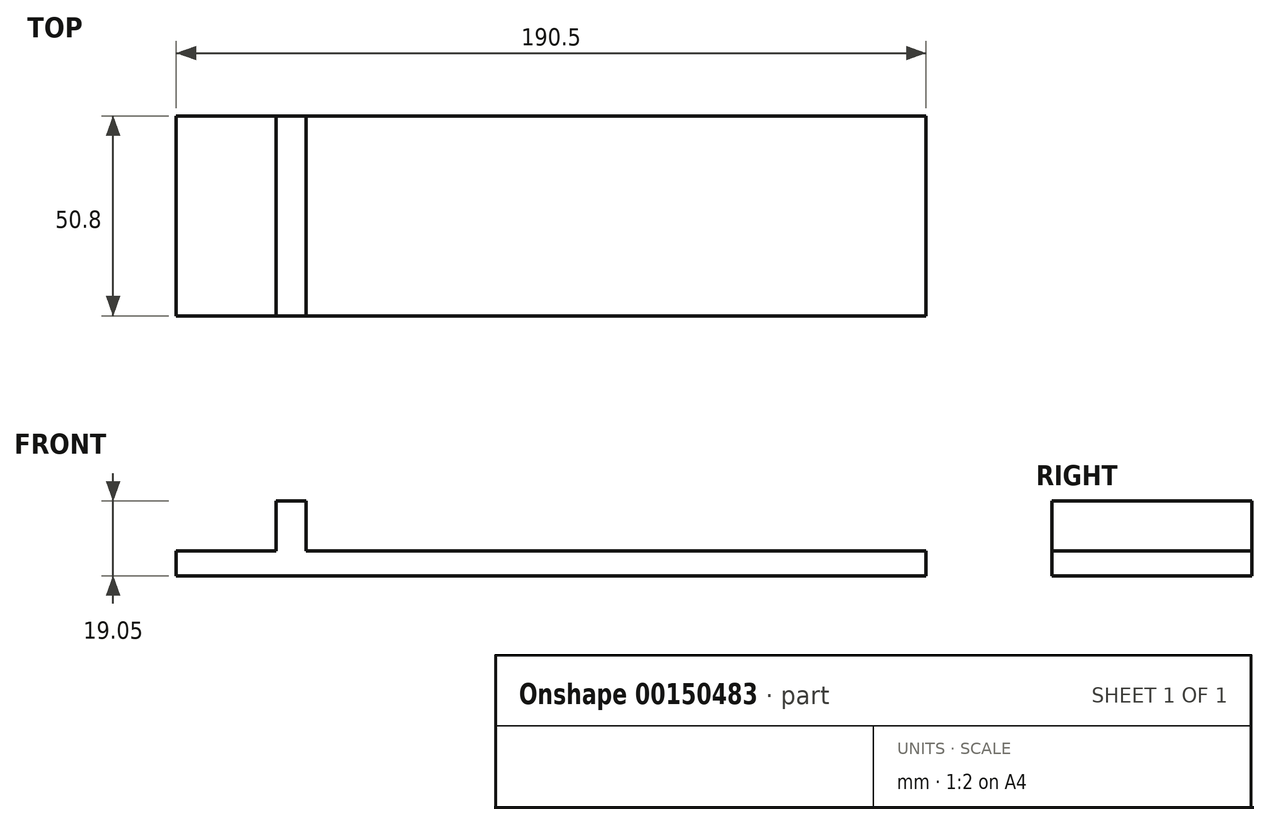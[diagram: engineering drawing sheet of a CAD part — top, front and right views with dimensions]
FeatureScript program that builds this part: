
annotation { "Feature Type Name" : "Feature", "Feature Type Description" : "" }
export const myFeature = defineFeature(function(context is Context, id is Id, definition is map)
    precondition{}
    {
        {
            var Q0;
            Q0=qCreatedBy(makeId("Front.planeOp"),FACE);
            var sketch = newSketch(context, id + "F0", { "sketchPlane" : qUnion([Q0])});
            skLineSegment(sketch, "E0", {"start": v(0, 0) * mm, "end": v(-95.25, 0) * mm});
            skLineSegment(sketch, "E1", {"start": v(-95.25, 0) * mm, "end": v(-95.25, 6.35) * mm});
            skLineSegment(sketch, "E2", {"start": v(-95.25, 6.35) * mm, "end": v(95.25, 6.35) * mm});
            skLineSegment(sketch, "E3", {"start": v(95.25, 6.35) * mm, "end": v(95.25, 0) * mm});
            skLineSegment(sketch, "E4", {"start": v(95.25, 0) * mm, "end": v(0, 0) * mm});
            skLineSegment(sketch, "E5", {"start": v(-69.85, 6.35) * mm, "end": v(-69.85, 19.05) * mm});
            skLineSegment(sketch, "E6", {"start": v(-69.85, 19.05) * mm, "end": v(-62.23, 19.05) * mm});
            skLineSegment(sketch, "E7", {"start": v(-62.23, 19.05) * mm, "end": v(-62.23, 6.35) * mm});
            skSolve(sketch);
        }
        {
            var Q0;
            Q0=makeQuery(id+"F0.imprint","IMPRINT",FACE,{"disambiguationData":[TD([[makeQuery(id+"F0.imprint","IMPRINT",EDGE,{"derivedFrom":sQuery(id+"F0.wireOp",EDGE,"E0")}),-1.0]])]});
            var Q1;
            {var subQ0=sQuery(id+"F0.wireOp",EDGE,"E5");Q1=makeQuery(id+"F0.imprint","IMPRINT",FACE,{"disambiguationData":[TD([[makeQuery(id+"F0.imprint","IMPRINT",EDGE,{"derivedFrom":subQ0}),-1.0]])]});}
            extrude(context, id + "F1", {"entities" : qUnion([Q0, Q1]), "depth" : 50.8 * mm});
        }
    });
